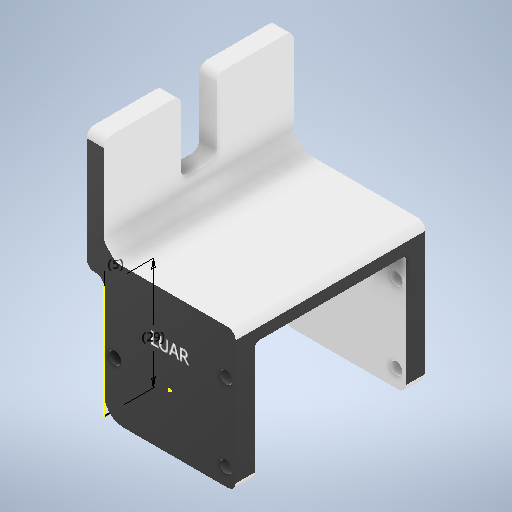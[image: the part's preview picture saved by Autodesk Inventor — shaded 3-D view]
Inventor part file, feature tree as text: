
AUTODESK INVENTOR PART (.ipt)
format: ipt  version: 2025.1 (Build 291241000, 241)  size: 414,208 bytes
history: native  units: mm
features: sketch x13, fillet x12, extrude x8, plane x1, chamfer x1
ambient origin geometry x8: Origin, YZ Plane, XZ Plane, XY Plane, X Axis, Y Axis, Z Axis, Center Point
bodies: Solid1 (feature_tree)
feature tree (35):
  sketch  "Sketch1"  dims[d0=34.0mm d1=29.0mm]
  extrude  "Extrusion1"  Depth=29.0mm
  sketch  "Sketch3"  dims[d4=3.2mm d5=20.0mm]
  sketch  "Sketch5"  dims[d6=2.5mm d7=14.5mm]
  extrude  "Extrusion3"  Depth=3.2mm
  extrude  "Extrusion4"  Depth=20.0mm
  extrude  "Extrusion5"  Depth=14.5mm
  sketch  "Sketch9"  dims[d30=2.0mm d31=0.0mm d32=5.0mm d33=0.0mm d34=5.0mm d35=44.0mm d36=0.0mm d37=-44.0mm d40=5.0mm d41=0.0mm d42=5.0mm d43=4.5mm d44=0.0mm d45=4.5mm d46=26.0mm d47=0.0mm d48=49.0mm d49=31.0mm d50=19.9mm d51=19.9mm d52=19.0mm]
  plane  "Work Plane1"
  extrude  "Extrusion6"  Depth=5.0mm TaperAngle=0.0deg
  sketch  "Sketch16"  dims[d55=2.0mm]
  extrude  "Extrusion7"  Depth=29.0mm
  extrude  "Extrusion8"  Depth=34.0mm
  extrude  "Extrusion9"  Depth=5.0mm TaperAngle=0.0deg
  fillet  "Fillet1"  Radius=5.0mm
  fillet  "Fillet2"  Radius=44.0mm
  fillet  "Fillet3"  [1 undecoded]
  fillet  "Fillet4"  Radius=5.0mm
  fillet  "Fillet5"  Radius=5.0mm
  fillet  "Fillet6"  Radius=4.5mm
  fillet  "Fillet7"  Radius=4.5mm
  chamfer  "Chamfer1"  Distance=26.0mm
  fillet  "Fillet8"  Radius=49.0mm
  fillet  "Fillet9"  Radius=31.0mm
  fillet  "Fillet10"  Radius=19.9mm
  fillet  "Fillet11"  Radius=19.9mm
  fillet  "Fillet12"  Radius=19.0mm
  sketch  "Sketch2"  dims[d2=3.2mm d3=3.2mm]
  sketch  "Sketch6"  dims[d8=28.7mm d10=5.0mm d11=0.0mm]
  sketch  "Sketch7"  dims[d26=5.0mm d27=29.0mm]
  sketch  "Sketch8"  dims[d28=5.0mm d29=34.0mm]
  sketch  "Sketch10"  dims[d53=26.0mm d54=0.0mm]
  sketch  "Sketch17"  dims[d56=2.0mm]
  sketch  "Sketch18"  dims[d57=5.0mm]
  sketch  "Sketch19"  dims[d58=5.0mm d59=2.0mm d60=2.0mm d61=2.0mm d68=3.2mm d69=3.2mm d70=3.2mm d71=3.0mm d72=2.0mm d73=45.0deg d74=2.0mm d75=2.0mm d76=2.0mm d77=1.0mm d78=1.0mm d79=9.2mm]
note: 1 required parameter value undecoded (feature->parameter linkage not recoverable at this tier; creation-order binding heuristic only, values carry confidence <= 0.55)
